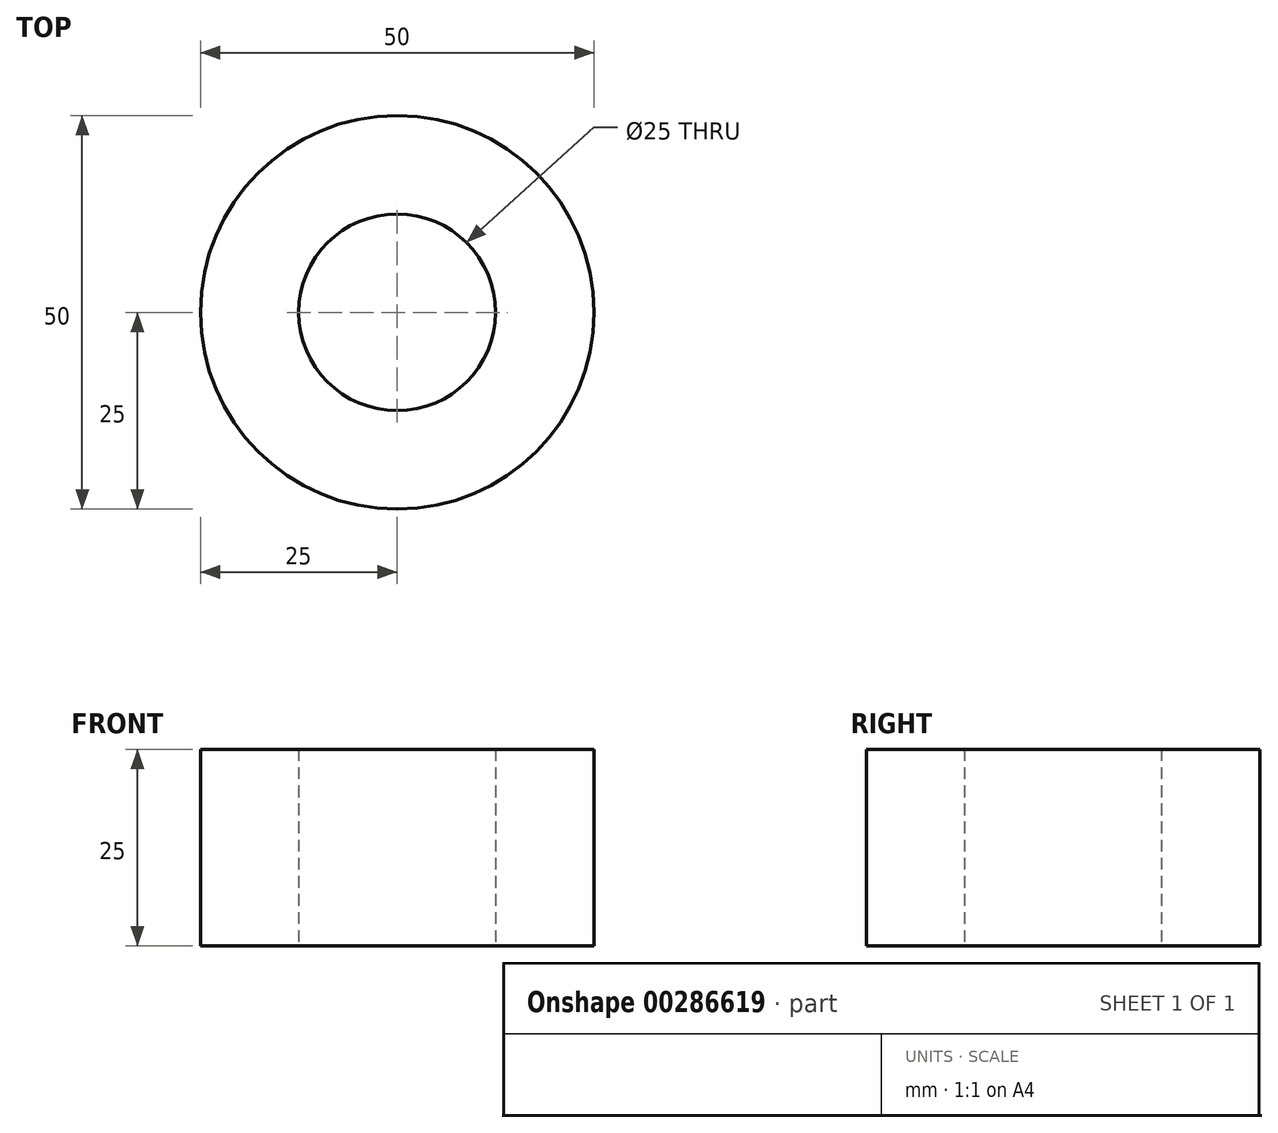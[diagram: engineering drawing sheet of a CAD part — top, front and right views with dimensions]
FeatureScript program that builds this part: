
annotation { "Feature Type Name" : "Feature", "Feature Type Description" : "" }
export const myFeature = defineFeature(function(context is Context, id is Id, definition is map)
    precondition{}
    {
        {
            var Q0;
            Q0=qCreatedBy(makeId("Top.planeOp"),FACE);
            var sketch = newSketch(context, id + "F0", { "sketchPlane" : qUnion([Q0])});
            skCircle(sketch, "E0", {"center": v(0, 0) * mm, "radius": 12.5 * mm});
            skCircle(sketch, "E1", {"center": v(0, 0) * mm, "radius": 25 * mm});
            skSolve(sketch);
        }
        {
            var Q0;
            Q0=makeQuery(id+"F0.imprint","IMPRINT",FACE,{"disambiguationData":[TD([[makeQuery(id+"F0.imprint","IMPRINT",EDGE,{"derivedFrom":sQuery(id+"F0.wireOp",EDGE,"E0")}),-1.0]])]});
            extrude(context, id + "F1", {"entities" : qUnion([Q0]), "depth" : 25 * mm});
        }
    });
